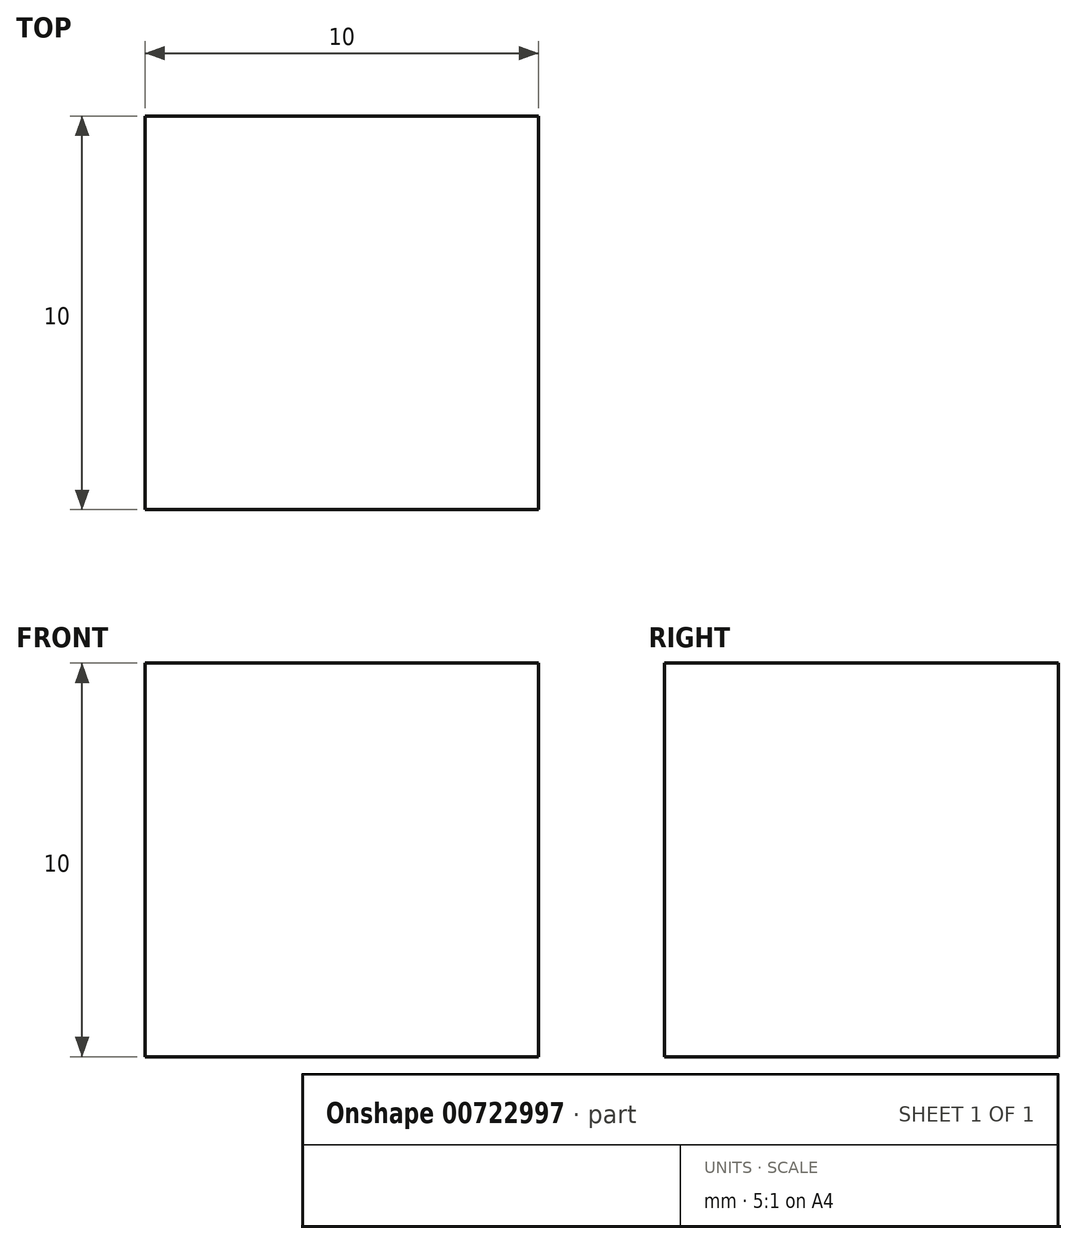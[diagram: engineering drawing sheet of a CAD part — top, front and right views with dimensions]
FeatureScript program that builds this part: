
annotation { "Feature Type Name" : "Feature", "Feature Type Description" : "" }
export const myFeature = defineFeature(function(context is Context, id is Id, definition is map)
    precondition{}
    {
        {
            var Q0;
            Q0=qCreatedBy(makeId("Front.planeOp"),FACE);
            var sketch = newSketch(context, id + "F0", { "sketchPlane" : qUnion([Q0])});
            skLineSegment(sketch, "E0.bottom", {"start": v(0, 0) * mm, "end": v(-10, 0) * mm});
            skLineSegment(sketch, "E0.top", {"start": v(0, 10) * mm, "end": v(-10, 10) * mm});
            skLineSegment(sketch, "E0.left", {"start": v(0, 0) * mm, "end": v(0, 10) * mm});
            skLineSegment(sketch, "E0.right", {"start": v(-10, 0) * mm, "end": v(-10, 10) * mm});
            skSolve(sketch);
        }
        {
            var Q0;
            Q0=makeQuery(id+"F0.imprint","IMPRINT",FACE,{"disambiguationData":[TD([[makeQuery(id+"F0.imprint","IMPRINT",EDGE,{"derivedFrom":sQuery(id+"F0.wireOp",EDGE,"E0.bottom")}),-1.0]])]});
            extrude(context, id + "F1", {"entities" : qUnion([Q0]), "depth" : 10 * mm, "offsetDistance" : 25 * mm});
        }
    });
